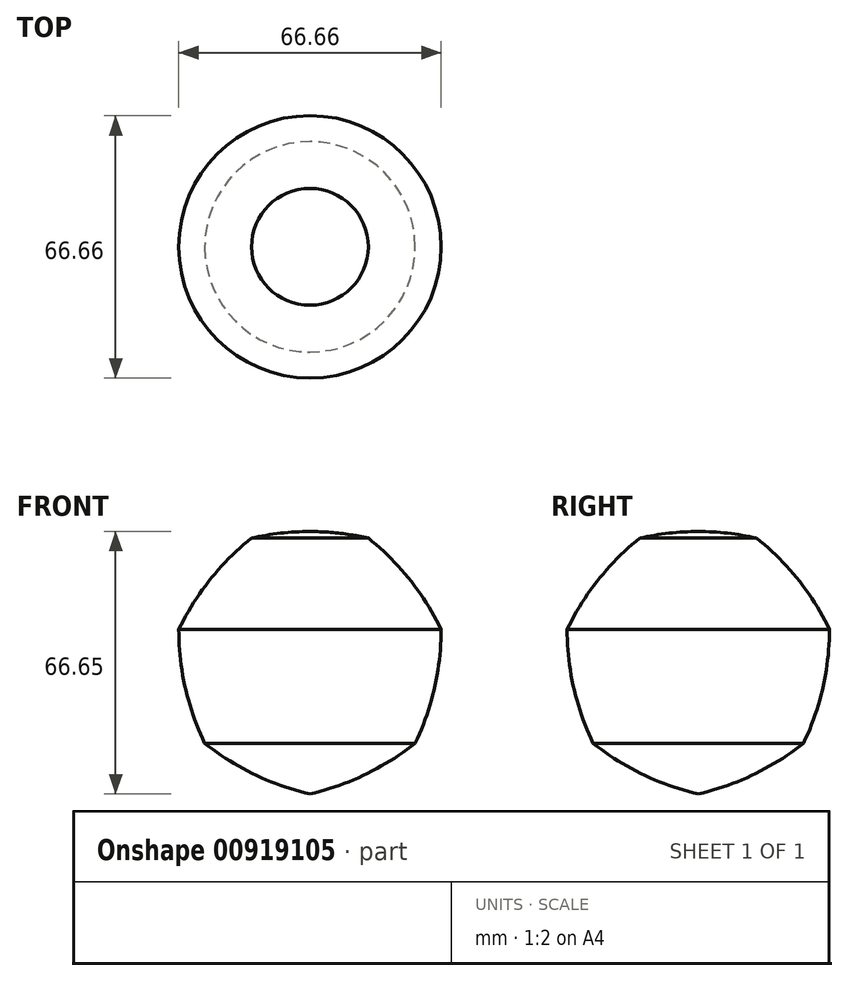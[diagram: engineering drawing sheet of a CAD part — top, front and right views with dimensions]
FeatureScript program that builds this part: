
annotation { "Feature Type Name" : "Feature", "Feature Type Description" : "" }
export const myFeature = defineFeature(function(context is Context, id is Id, definition is map)
    precondition{}
    {
        {
            var Q0;
            Q0=qCreatedBy(makeId("Front.planeOp"),FACE);
            var sketch = newSketch(context, id + "F0", { "sketchPlane" : qUnion([Q0])});
            skCircle(sketch, "E0.cCircle", {"center": v(0, 0) * mm, "radius": 30.8 * mm, "construction": true});
            skLineSegment(sketch, "E0.0", {"start": v(-14.83, 30.8) * mm, "end": v(14.83, 30.8) * mm});
            skLineSegment(sketch, "E0.1", {"start": v(14.83, 30.8) * mm, "end": v(33.33, 7.6) * mm});
            skLineSegment(sketch, "E0.2", {"start": v(33.33, 7.6) * mm, "end": v(26.73, -21.31) * mm});
            skLineSegment(sketch, "E0.3", {"start": v(26.73, -21.31) * mm, "end": v(0, -34.18) * mm});
            skLineSegment(sketch, "E0.4", {"start": v(0, -34.18) * mm, "end": v(-26.73, -21.31) * mm});
            skLineSegment(sketch, "E0.5", {"start": v(-26.73, -21.31) * mm, "end": v(-33.33, 7.6) * mm});
            skLineSegment(sketch, "E0.6", {"start": v(-33.33, 7.6) * mm, "end": v(-14.83, 30.8) * mm});
            skPoint(sketch, "E0.0.midPoint", {"position": v(0, 30.8) * mm});
            skPoint(sketch, "E1", {"position": v(24.08, 19.2) * mm});
            skLineSegment(sketch, "E2", {"start": v(0, -34.18) * mm, "end": v(0, 30.8) * mm});
            skCircle(sketch, "E3", {"center": v(-14.83, 30.8) * mm, "radius": 66.65 * mm});
            skCircle(sketch, "E4", {"center": v(14.83, 30.8) * mm, "radius": 66.65 * mm});
            skCircle(sketch, "E5", {"center": v(33.33, 7.6) * mm, "radius": 66.65 * mm});
            skCircle(sketch, "E6", {"center": v(26.73, -21.31) * mm, "radius": 66.65 * mm});
            skCircle(sketch, "E7", {"center": v(0, -34.18) * mm, "radius": 66.65 * mm});
            skCircle(sketch, "E8", {"center": v(-26.73, -21.31) * mm, "radius": 66.65 * mm});
            skCircle(sketch, "E9", {"center": v(-33.33, 7.6) * mm, "radius": 66.65 * mm});
            skLineSegment(sketch, "E10", {"start": v(0, 30.8) * mm, "end": v(0, 32.47) * mm});
            skSolve(sketch);
        }
        {
            var Q0;
            Q0=makeQuery(id+"F0.imprint","IMPRINT",FACE,{"disambiguationData":[TD([[makeQuery(id+"F0.imprint","IMPRINT",EDGE,{"derivedFrom":sQuery(id+"F0.wireOp",EDGE,"E0.4")}),-1.0]])]});
            var Q1;
            {var subQ0=sQuery(id+"F0.wireOp",EDGE,"E0.4");Q1=makeQuery(id+"F0.imprint","IMPRINT",FACE,{"disambiguationData":[TD([[makeQuery(id+"F0.imprint","IMPRINT",EDGE,{"derivedFrom":subQ0}),1.0]])]});}
            var Q2;
            {var subQ0=sQuery(id+"F0.wireOp",EDGE,"E0.5");Q2=makeQuery(id+"F0.imprint","IMPRINT",FACE,{"disambiguationData":[TD([[makeQuery(id+"F0.imprint","IMPRINT",EDGE,{"derivedFrom":subQ0}),1.0]])]});}
            var Q3;
            {var subQ0=sQuery(id+"F0.wireOp",EDGE,"E0.6");Q3=makeQuery(id+"F0.imprint","IMPRINT",FACE,{"disambiguationData":[TD([[makeQuery(id+"F0.imprint","IMPRINT",EDGE,{"derivedFrom":subQ0}),1.0]])]});}
            var Q4;
            {var subQ3=sQuery(id+"F0.wireOp",EDGE,"E10");Q4=makeQuery(id+"F0.imprint","IMPRINT",FACE,{"disambiguationData":[TD([[makeQuery(id+"F0.imprint","IMPRINT",EDGE,{"derivedFrom":subQ3}),1.0]])]});}
            var Q5;
            Q5=sQuery(id+"F0.wireOp",EDGE,"E2");
            revolve(context, id + "F1", {"surfaceOperationType" : NewSurfaceOperationType.NEW, "entities" : qUnion([Q0, Q1, Q2, Q3, Q4]), "axis" : qUnion([Q5]), "revolveType" : RevolveType.FULL});
        }
    });
